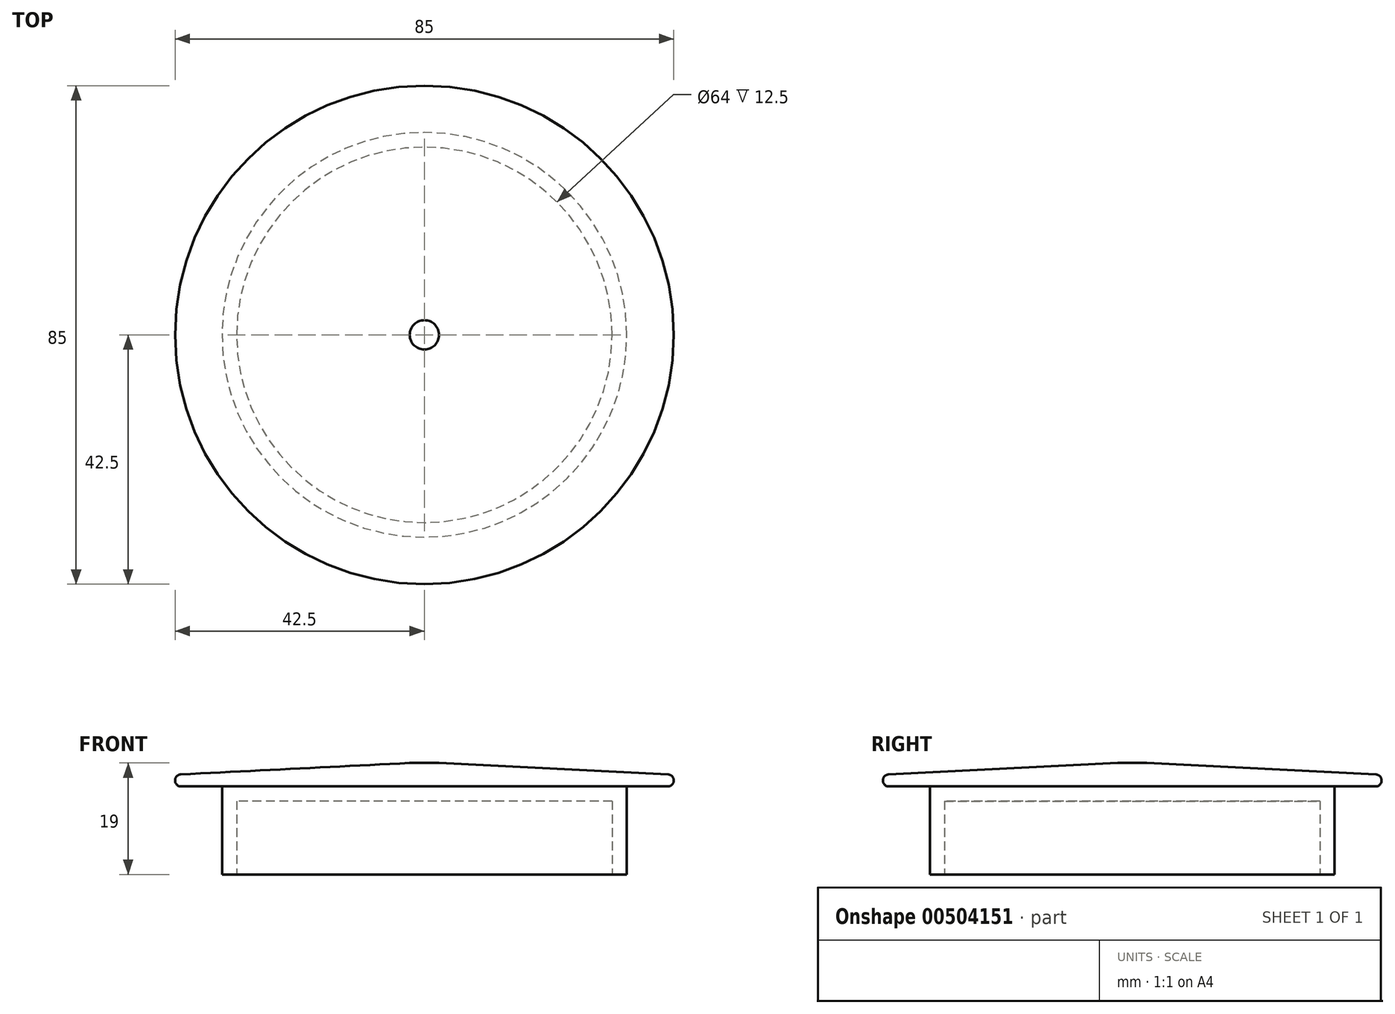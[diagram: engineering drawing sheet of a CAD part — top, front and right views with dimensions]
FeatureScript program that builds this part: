
annotation { "Feature Type Name" : "Feature", "Feature Type Description" : "" }
export const myFeature = defineFeature(function(context is Context, id is Id, definition is map)
    precondition{}
    {
        {
            var Q0;
            Q0=qCreatedBy(makeId("Top.planeOp"),FACE);
            var sketch = newSketch(context, id + "F0", { "sketchPlane" : qUnion([Q0])});
            skCircle(sketch, "E0", {"center": v(0, 0) * mm, "radius": 34.5 * mm});
            skSolve(sketch);
        }
        {
            var Q0;
            Q0=makeQuery(id+"F0.imprint","IMPRINT",FACE,{"disambiguationData":[TD([[makeQuery(id+"F0.imprint","IMPRINT",EDGE,{"derivedFrom":sQuery(id+"F0.wireOp",EDGE,"E0")}),1.0]])]});
            extrude(context, id + "F1", {"entities" : qUnion([Q0]), "depth" : 15 * mm});
        }
        {
            var Q0;
            Q0=makeQuery(id+"F1.opExtrude","CAP_FACE",FACE,{"disambiguationData":[OSD([sQuery(id+"F0.wireOp",EDGE,"E0")])],"isStart":true});
            shell(context, id + "F2", {"entities" : qUnion([Q0]), "thickness" : 2.5 * mm});
        }
        {
            var Q0;
            Q0=makeQuery(id+"F1.opExtrude","CAP_FACE",FACE,{"disambiguationData":[OSD([sQuery(id+"F0.wireOp",EDGE,"E0")])],"isStart":false});
            var sketch = newSketch(context, id + "F3", { "sketchPlane" : qUnion([Q0])});
            skCircle(sketch, "E1", {"center": v(0, 0) * mm, "radius": 42.5 * mm});
            skSolve(sketch);
        }
        {
            var Q0;
            Q0=makeQuery(id+"F3.imprint","IMPRINT",FACE,{"disambiguationData":[TD([[makeQuery(id+"F3.imprint","IMPRINT",EDGE,{"derivedFrom":sQuery(id+"F3.wireOp",EDGE,"E1")}),1.0]])]});
            var Q1;
            Q1=makeQuery(id+"F3.imprint","IMPRINT",FACE,{"disambiguationData":[TD([[makeQuery(id+"F3.imprint","IMPRINT",EDGE,{"derivedFrom":makeQuery(id+"F1.opExtrude","CAP_EDGE",EDGE,{"disambiguationData":[OSD([sQuery(id+"F0.wireOp",EDGE,"E0")])],"isStart":false})}),1.0]])]});
            var Q2;
            Q2=sQuery(id+"F3.wireOp",EDGE,"E1");
            extrude(context, id + "F4", {"entities" : qUnion([Q0, Q1]), "operationType" : NewBodyOperationType.ADD, "surfaceEntities" : qUnion([Q2]), "depth" : 2 * mm});
        }
        {
            var Q0;
            Q0=makeQuery(id+"F4.opExtrude","CAP_FACE",FACE,{"disambiguationData":[OSD([sQuery(id+"F3.wireOp",EDGE,"E1")])],"isStart":false});
            cPlane(context, id + "F5", {"entities" : qUnion([Q0]), "cplaneType" : CPlaneType.OFFSET, "offset" : 2 * mm, "width" : 150 * mm, "height" : 150 * mm});
        }
        {
            var Q0;
            Q0=qCreatedBy(id+"F5.planeOp",FACE);
            var sketch = newSketch(context, id + "F6", { "sketchPlane" : qUnion([Q0])});
            skCircle(sketch, "E2", {"center": v(0, 0) * mm, "radius": 2.5 * mm});
            skSolve(sketch);
        }
        {
            var Q1;
            Q1=makeQuery(id+"F4.opExtrude","CAP_FACE",FACE,{"disambiguationData":[OSD([sQuery(id+"F3.wireOp",EDGE,"E1")])],"isStart":false});
            var Q2;
            Q2=makeQuery(id+"F6.imprint","IMPRINT",FACE,{"disambiguationData":[TD([[makeQuery(id+"F6.imprint","IMPRINT",EDGE,{"derivedFrom":sQuery(id+"F6.wireOp",EDGE,"E2")}),1.0]])]});
            loft(context, id + "F7", {"operationType" : NewBodyOperationType.ADD, "sheetProfilesArray" : [{ "sheetProfileEntities" : qUnion([Q1]) }, { "sheetProfileEntities" : qUnion([Q2]) }]});
        }
        {
            var Q0;
            {var subQ0=sQuery(id+"F3.wireOp",EDGE,"E1");Q0=makeQuery(id+"F7.boolean.opBoolean","MERGE",EDGE,{"derivedFrom":[makeQuery(id+"F4.opExtrude","CAP_EDGE",EDGE,{"disambiguationData":[OSD([subQ0])],"isStart":false}),makeQuery(id+"F7.opLoft","MID_CAP_EDGE",EDGE,{"disambiguationData":[OSD([subQ0])],"capPos":0.0})]});}
            fillet(context, id + "F8", {"entities" : qUnion([Q0]), "radius" : 1 * mm, "tangentPropagation" : true, "allowEdgeOverflow" : false});
        }
        {
            var Q0;
            Q0=makeQuery(id+"F4.opExtrude","CAP_EDGE",EDGE,{"disambiguationData":[OSD([sQuery(id+"F3.wireOp",EDGE,"E1")])],"isStart":true});
            fillet(context, id + "F9", {"entities" : qUnion([Q0]), "radius" : 1 * mm, "tangentPropagation" : true, "allowEdgeOverflow" : false});
        }
    });
